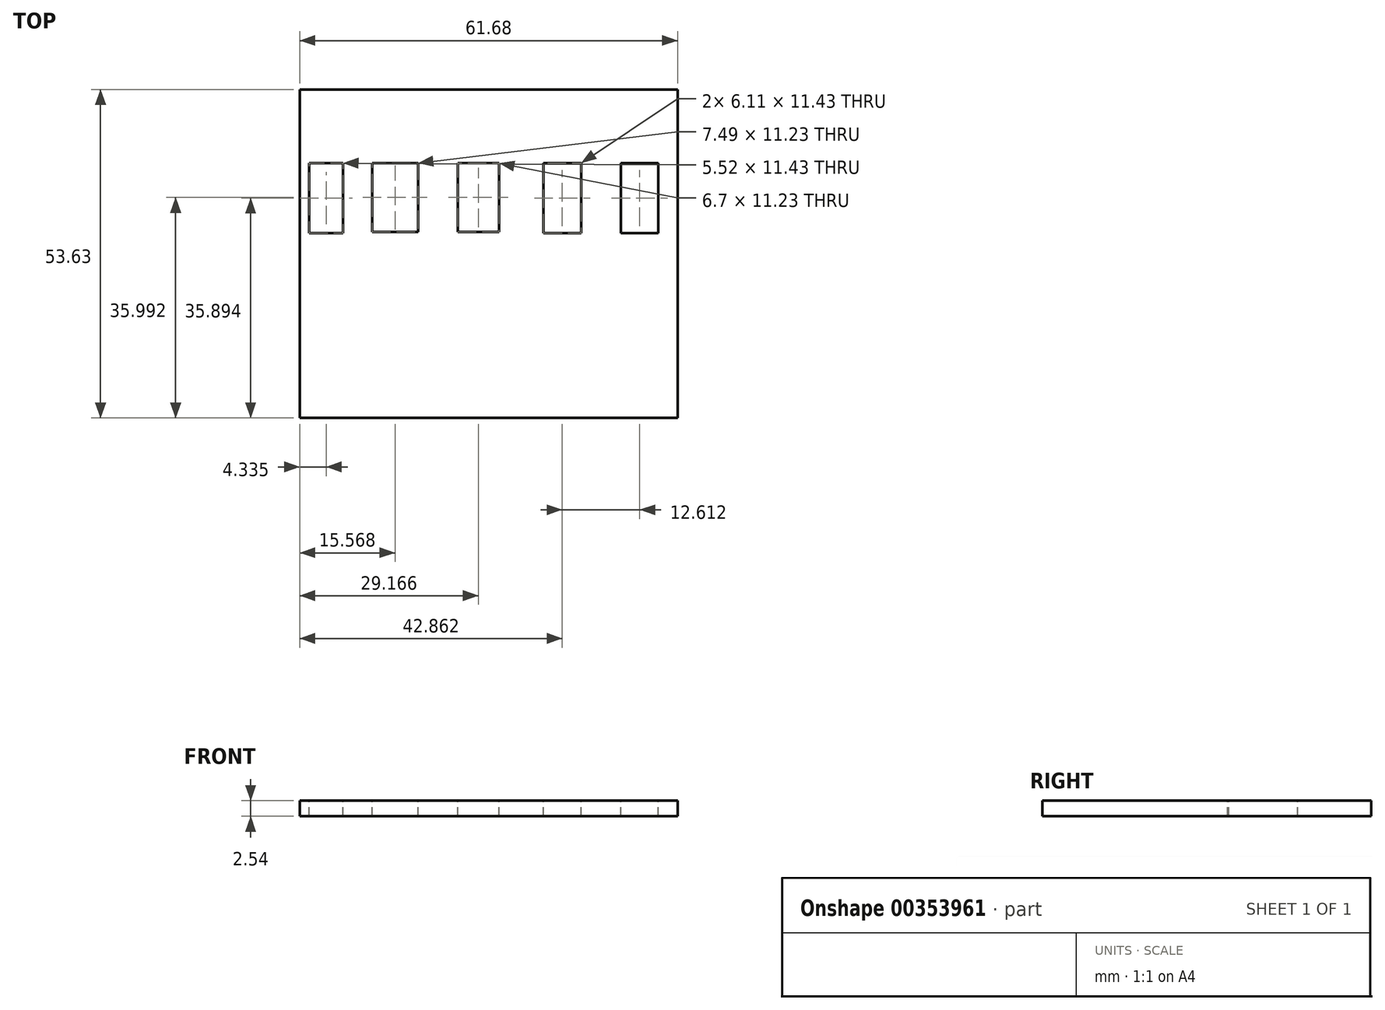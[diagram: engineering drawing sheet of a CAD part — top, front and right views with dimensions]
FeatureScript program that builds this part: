
annotation { "Feature Type Name" : "Feature", "Feature Type Description" : "" }
export const myFeature = defineFeature(function(context is Context, id is Id, definition is map)
    precondition{}
    {
        {
            var Q0;
            Q0=qCreatedBy(makeId("Top.planeOp"),FACE);
            var sketch = newSketch(context, id + "F0", { "sketchPlane" : qUnion([Q0])});
            skLineSegment(sketch, "E0.bottom", {"start": v(0, 0) * mm, "end": v(61.68, 0) * mm});
            skLineSegment(sketch, "E0.top", {"start": v(0, -53.63) * mm, "end": v(61.68, -53.63) * mm});
            skLineSegment(sketch, "E0.left", {"start": v(0, 0) * mm, "end": v(0, -53.63) * mm});
            skLineSegment(sketch, "E0.right", {"start": v(61.68, 0) * mm, "end": v(61.68, -53.63) * mm});
            skSolve(sketch);
        }
        {
            var Q0;
            Q0 = qSketchRegion(id + "F0", true);
            extrude(context, id + "F1", {"entities" : qUnion([Q0]), "depth" : 2.54 * mm});
        }
        {
            var Q0;
            Q0=makeQuery(id+"F1.opExtrude","CAP_FACE",FACE,{"disambiguationData":[OSD([sQuery(id+"F0.wireOp",EDGE,"E0.bottom"),sQuery(id+"F0.wireOp",EDGE,"E0.top"),sQuery(id+"F0.wireOp",EDGE,"E0.left"),sQuery(id+"F0.wireOp",EDGE,"E0.right")])],"isStart":false});
            var sketch = newSketch(context, id + "F2", { "sketchPlane" : qUnion([Q0])});
            skLineSegment(sketch, "E1.bottom", {"start": v(11.82, -12.02) * mm, "end": v(19.31, -12.02) * mm});
            skLineSegment(sketch, "E1.top", {"start": v(11.82, -23.25) * mm, "end": v(19.31, -23.25) * mm});
            skLineSegment(sketch, "E1.left", {"start": v(11.82, -12.02) * mm, "end": v(11.82, -23.25) * mm});
            skLineSegment(sketch, "E1.right", {"start": v(19.31, -12.02) * mm, "end": v(19.31, -23.25) * mm});
            skLineSegment(sketch, "E2.bottom", {"start": v(25.82, -12.02) * mm, "end": v(32.52, -12.02) * mm});
            skLineSegment(sketch, "E2.top", {"start": v(25.82, -23.25) * mm, "end": v(32.52, -23.25) * mm});
            skLineSegment(sketch, "E2.left", {"start": v(25.82, -12.02) * mm, "end": v(25.82, -23.25) * mm});
            skLineSegment(sketch, "E2.right", {"start": v(32.52, -12.02) * mm, "end": v(32.52, -23.25) * mm});
            skLineSegment(sketch, "E3.bottom", {"start": v(39.8, -12.02) * mm, "end": v(45.92, -12.02) * mm});
            skLineSegment(sketch, "E3.top", {"start": v(39.8, -23.45) * mm, "end": v(45.92, -23.45) * mm});
            skLineSegment(sketch, "E3.left", {"start": v(39.8, -12.02) * mm, "end": v(39.8, -23.45) * mm});
            skLineSegment(sketch, "E3.right", {"start": v(45.92, -12.02) * mm, "end": v(45.92, -23.45) * mm});
            skLineSegment(sketch, "E4.bottom", {"start": v(52.42, -12.02) * mm, "end": v(58.53, -12.02) * mm});
            skLineSegment(sketch, "E4.top", {"start": v(52.42, -23.45) * mm, "end": v(58.53, -23.45) * mm});
            skLineSegment(sketch, "E4.left", {"start": v(52.42, -12.02) * mm, "end": v(52.42, -23.45) * mm});
            skLineSegment(sketch, "E4.right", {"start": v(58.53, -12.02) * mm, "end": v(58.53, -23.45) * mm});
            skLineSegment(sketch, "E5.bottom", {"start": v(7.1, -12.02) * mm, "end": v(1.58, -12.02) * mm});
            skLineSegment(sketch, "E5.top", {"start": v(7.1, -23.45) * mm, "end": v(1.58, -23.45) * mm});
            skLineSegment(sketch, "E5.left", {"start": v(7.1, -12.02) * mm, "end": v(7.1, -23.45) * mm});
            skLineSegment(sketch, "E5.right", {"start": v(1.58, -12.02) * mm, "end": v(1.58, -23.45) * mm});
            skSolve(sketch);
        }
        {
            var Q0;
            Q0 = qSketchRegion(id + "F2", true);
            extrude(context, id + "F3", {"entities" : qUnion([Q0]), "operationType" : NewBodyOperationType.REMOVE, "oppositeDirection" : true, "depth" : 25.4 * mm});
        }
    });
